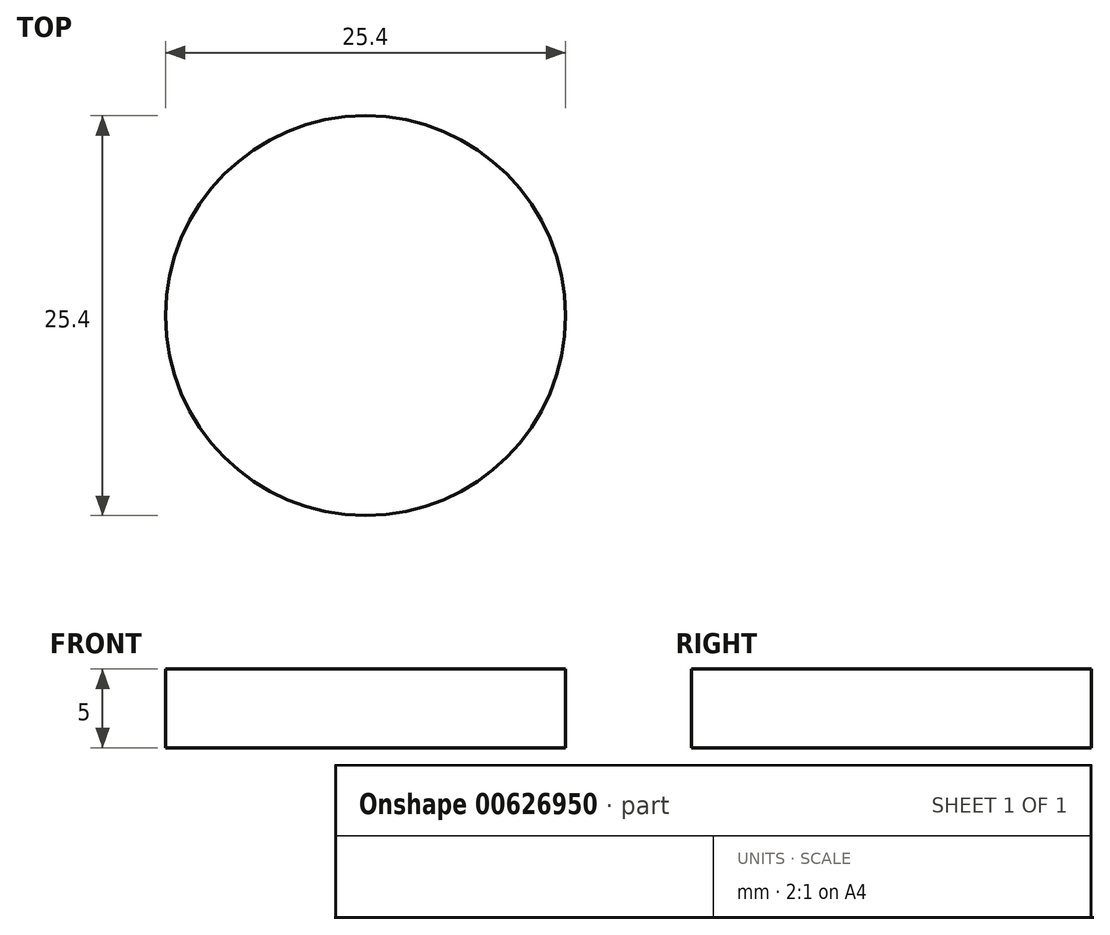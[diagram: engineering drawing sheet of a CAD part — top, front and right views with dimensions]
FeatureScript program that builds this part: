
annotation { "Feature Type Name" : "Feature", "Feature Type Description" : "" }
export const myFeature = defineFeature(function(context is Context, id is Id, definition is map)
    precondition{}
    {
        {
            var Q0;
            Q0=qCreatedBy(makeId("Top.planeOp"),FACE);
            var sketch = newSketch(context, id + "F0", { "sketchPlane" : qUnion([Q0])});
            skCircle(sketch, "E0", {"center": v(0, 0) * mm, "radius": 12.7 * mm});
            skSolve(sketch);
        }
        {
            var Q0;
            Q0=makeQuery(id+"F0.imprint","IMPRINT",FACE,{"disambiguationData":[TD([[makeQuery(id+"F0.imprint","IMPRINT",EDGE,{"derivedFrom":sQuery(id+"F0.wireOp",EDGE,"E0")}),1.0]])]});
            extrude(context, id + "F1", {"entities" : qUnion([Q0]), "flatOperationType" : FlatOperationType.REMOVE, "depth" : 5 * mm, "offsetDistance" : 25 * mm, "domain" : OperationDomain.MODEL});
        }
    });
